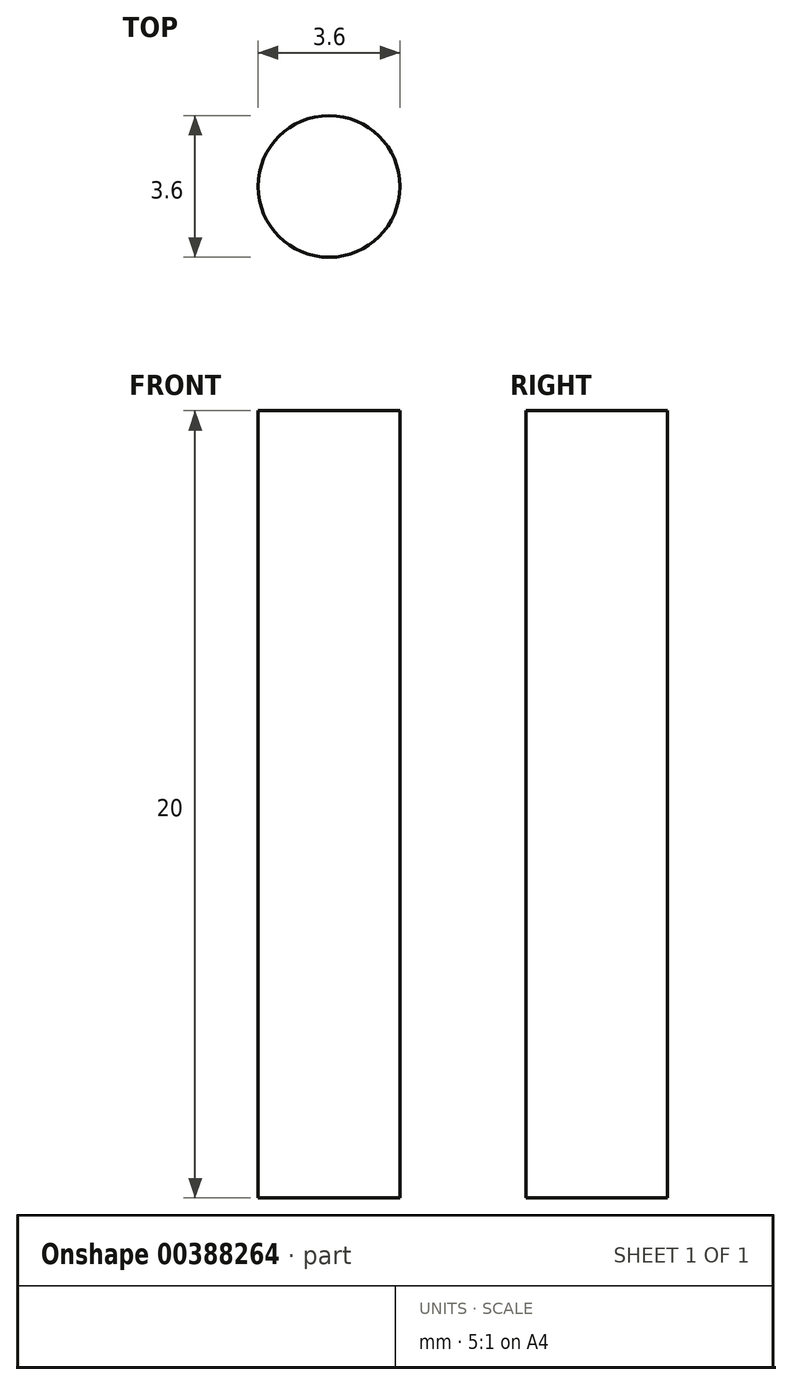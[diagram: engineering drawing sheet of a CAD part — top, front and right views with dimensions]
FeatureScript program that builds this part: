
annotation { "Feature Type Name" : "Feature", "Feature Type Description" : "" }
export const myFeature = defineFeature(function(context is Context, id is Id, definition is map)
    precondition{}
    {
        {
            var Q0;
            Q0=qCreatedBy(makeId("Top.planeOp"),FACE);
            var sketch = newSketch(context, id + "F0", { "sketchPlane" : qUnion([Q0])});
            skCircle(sketch, "E0", {"center": v(0, 0) * mm, "radius": 1.8 * mm});
            skSolve(sketch);
        }
        {
            var Q0;
            Q0 = qSketchRegion(id + "F0", true);
            extrude(context, id + "F1", {"entities" : qUnion([Q0]), "depth" : 20 * mm});
        }
    });
